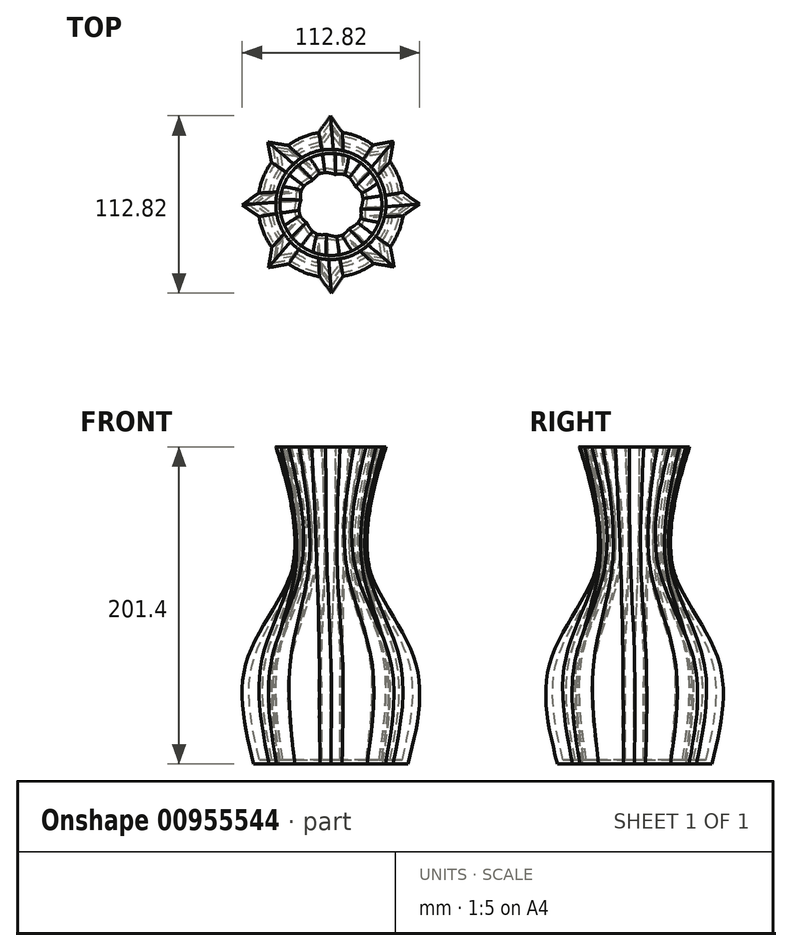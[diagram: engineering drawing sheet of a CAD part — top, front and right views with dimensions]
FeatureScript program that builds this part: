
annotation { "Feature Type Name" : "Feature", "Feature Type Description" : "" }
export const myFeature = defineFeature(function(context is Context, id is Id, definition is map)
    precondition{}
    {
        {
            var Q0;
            Q0=qCreatedBy(makeId("Top.planeOp"),FACE);
            var sketch = newSketch(context, id + "F0", { "sketchPlane" : qUnion([Q0])});
            skCircle(sketch, "E0", {"center": v(0, 0) * mm, "radius": 40 * mm});
            skLineSegment(sketch, "E1", {"start": v(-7.07, 39.37) * mm, "end": v(0, 49.06) * mm});
            skLineSegment(sketch, "E2", {"start": v(0, 49.06) * mm, "end": v(7.07, 39.37) * mm});
            skLineSegment(sketch, "E3.1.0", {"start": v(-34.7, 34.7) * mm, "end": v(-22.84, 32.84) * mm});
            skLineSegment(sketch, "E3.1.1", {"start": v(-32.84, 22.84) * mm, "end": v(-34.7, 34.7) * mm});
            skLineSegment(sketch, "E3.2.0", {"start": v(-49.06, 0) * mm, "end": v(-39.37, 7.07) * mm});
            skLineSegment(sketch, "E3.2.1", {"start": v(-39.37, -7.07) * mm, "end": v(-49.06, 0) * mm});
            skLineSegment(sketch, "E3.3.0", {"start": v(-34.7, -34.7) * mm, "end": v(-32.84, -22.84) * mm});
            skLineSegment(sketch, "E3.3.1", {"start": v(-22.84, -32.84) * mm, "end": v(-34.7, -34.7) * mm});
            skLineSegment(sketch, "E3.4.0", {"start": v(0, -49.06) * mm, "end": v(-7.07, -39.37) * mm});
            skLineSegment(sketch, "E3.4.1", {"start": v(7.07, -39.37) * mm, "end": v(0, -49.06) * mm});
            skLineSegment(sketch, "E3.5.0", {"start": v(34.7, -34.7) * mm, "end": v(22.84, -32.84) * mm});
            skLineSegment(sketch, "E3.5.1", {"start": v(32.84, -22.84) * mm, "end": v(34.7, -34.7) * mm});
            skLineSegment(sketch, "E3.6.0", {"start": v(49.06, 0) * mm, "end": v(39.37, -7.07) * mm});
            skLineSegment(sketch, "E3.6.1", {"start": v(39.37, 7.07) * mm, "end": v(49.06, 0) * mm});
            skLineSegment(sketch, "E3.7.0", {"start": v(34.7, 34.7) * mm, "end": v(32.84, 22.84) * mm});
            skLineSegment(sketch, "E3.7.1", {"start": v(22.84, 32.84) * mm, "end": v(34.7, 34.7) * mm});
            skSolve(sketch);
        }
        {
            var Q0;
            Q0=qCreatedBy(makeId("Top.planeOp"),FACE);
            cPlane(context, id + "F1", {"entities" : qUnion([Q0]), "cplaneType" : CPlaneType.OFFSET, "offset" : 66.3 * mm, "width" : 150 * mm, "height" : 150 * mm});
        }
        {
            var Q0;
            Q0=qCreatedBy(id+"F1.planeOp",FACE);
            var sketch = newSketch(context, id + "F2", { "sketchPlane" : qUnion([Q0])});
            skCircle(sketch, "E4", {"center": v(0, 0) * mm, "radius": 44.4 * mm});
            skLineSegment(sketch, "E5", {"start": v(-7.4, 43.77) * mm, "end": v(0, 53.22) * mm});
            skLineSegment(sketch, "E6", {"start": v(0, 53.22) * mm, "end": v(7.4, 43.77) * mm});
            skLineSegment(sketch, "E7.1.0", {"start": v(-37.63, 37.63) * mm, "end": v(-25.72, 36.19) * mm});
            skLineSegment(sketch, "E7.1.1", {"start": v(-36.19, 25.72) * mm, "end": v(-37.63, 37.63) * mm});
            skLineSegment(sketch, "E7.2.0", {"start": v(-53.22, 0) * mm, "end": v(-43.77, 7.4) * mm});
            skLineSegment(sketch, "E7.2.1", {"start": v(-43.77, -7.4) * mm, "end": v(-53.22, 0) * mm});
            skLineSegment(sketch, "E7.3.0", {"start": v(-37.63, -37.63) * mm, "end": v(-36.19, -25.72) * mm});
            skLineSegment(sketch, "E7.3.1", {"start": v(-25.72, -36.19) * mm, "end": v(-37.63, -37.63) * mm});
            skLineSegment(sketch, "E7.4.0", {"start": v(0, -53.22) * mm, "end": v(-7.4, -43.77) * mm});
            skLineSegment(sketch, "E7.4.1", {"start": v(7.4, -43.77) * mm, "end": v(0, -53.22) * mm});
            skLineSegment(sketch, "E7.5.0", {"start": v(37.63, -37.63) * mm, "end": v(25.72, -36.19) * mm});
            skLineSegment(sketch, "E7.5.1", {"start": v(36.19, -25.72) * mm, "end": v(37.63, -37.63) * mm});
            skLineSegment(sketch, "E7.6.0", {"start": v(53.22, 0) * mm, "end": v(43.77, -7.4) * mm});
            skLineSegment(sketch, "E7.6.1", {"start": v(43.77, 7.4) * mm, "end": v(53.22, 0) * mm});
            skLineSegment(sketch, "E7.7.0", {"start": v(37.63, 37.63) * mm, "end": v(36.19, 25.72) * mm});
            skLineSegment(sketch, "E7.7.1", {"start": v(25.72, 36.19) * mm, "end": v(37.63, 37.63) * mm});
            skSolve(sketch);
        }
        {
            var Q0;
            Q0=qCreatedBy(id+"F1.planeOp",FACE);
            cPlane(context, id + "F3", {"entities" : qUnion([Q0]), "cplaneType" : CPlaneType.OFFSET, "offset" : 56.1 * mm, "width" : 150 * mm, "height" : 150 * mm});
        }
        {
            var Q0;
            Q0=qCreatedBy(id+"F3.planeOp",FACE);
            var sketch = newSketch(context, id + "F4", { "sketchPlane" : qUnion([Q0])});
            skCircle(sketch, "E8", {"center": v(0, 0) * mm, "radius": 25 * mm});
            skSolve(sketch);
        }
        {
            var Q0;
            Q0=qCreatedBy(id+"F3.planeOp",FACE);
            cPlane(context, id + "F5", {"entities" : qUnion([Q0]), "cplaneType" : CPlaneType.OFFSET, "offset" : 79 * mm, "width" : 150 * mm, "height" : 150 * mm});
        }
        {
            var Q0;
            Q0=qCreatedBy(id+"F5.planeOp",FACE);
            var sketch = newSketch(context, id + "F6", { "sketchPlane" : qUnion([Q0])});
            skCircle(sketch, "E9", {"center": v(0, 0) * mm, "radius": 35 * mm});
            skSolve(sketch);
        }
        {
            var Q0;
            Q0 = qSketchRegion(id + "F0", true);
            var Q1;
            Q1 = qSketchRegion(id + "F2", true);
            var Q2;
            Q2 = qSketchRegion(id + "F4", true);
            var Q3;
            Q3 = qSketchRegion(id + "F6", true);
            loft(context, id + "F7", {"sheetProfilesArray" : [{ "sheetProfileEntities" : qUnion([Q0]) }, { "sheetProfileEntities" : qUnion([Q1]) }, { "sheetProfileEntities" : qUnion([Q2]) }, { "sheetProfileEntities" : qUnion([Q3]) }]});
        }
        {
            var Q0;
            Q0=makeQuery(id+"F7.opLoft","CAP_FACE",FACE,{"disambiguationData":[OSD([makeQuery(id+"F6.imprint","IMPRINT",FACE,{"disambiguationData":[TD([[makeQuery(id+"F6.imprint","IMPRINT",EDGE,{"derivedFrom":sQuery(id+"F6.wireOp",EDGE,"E9")}),1.0]])]})])],"isStart":true});
            shell(context, id + "F8", {"entities" : qUnion([Q0]), "thickness" : 2.5 * mm});
        }
    });
